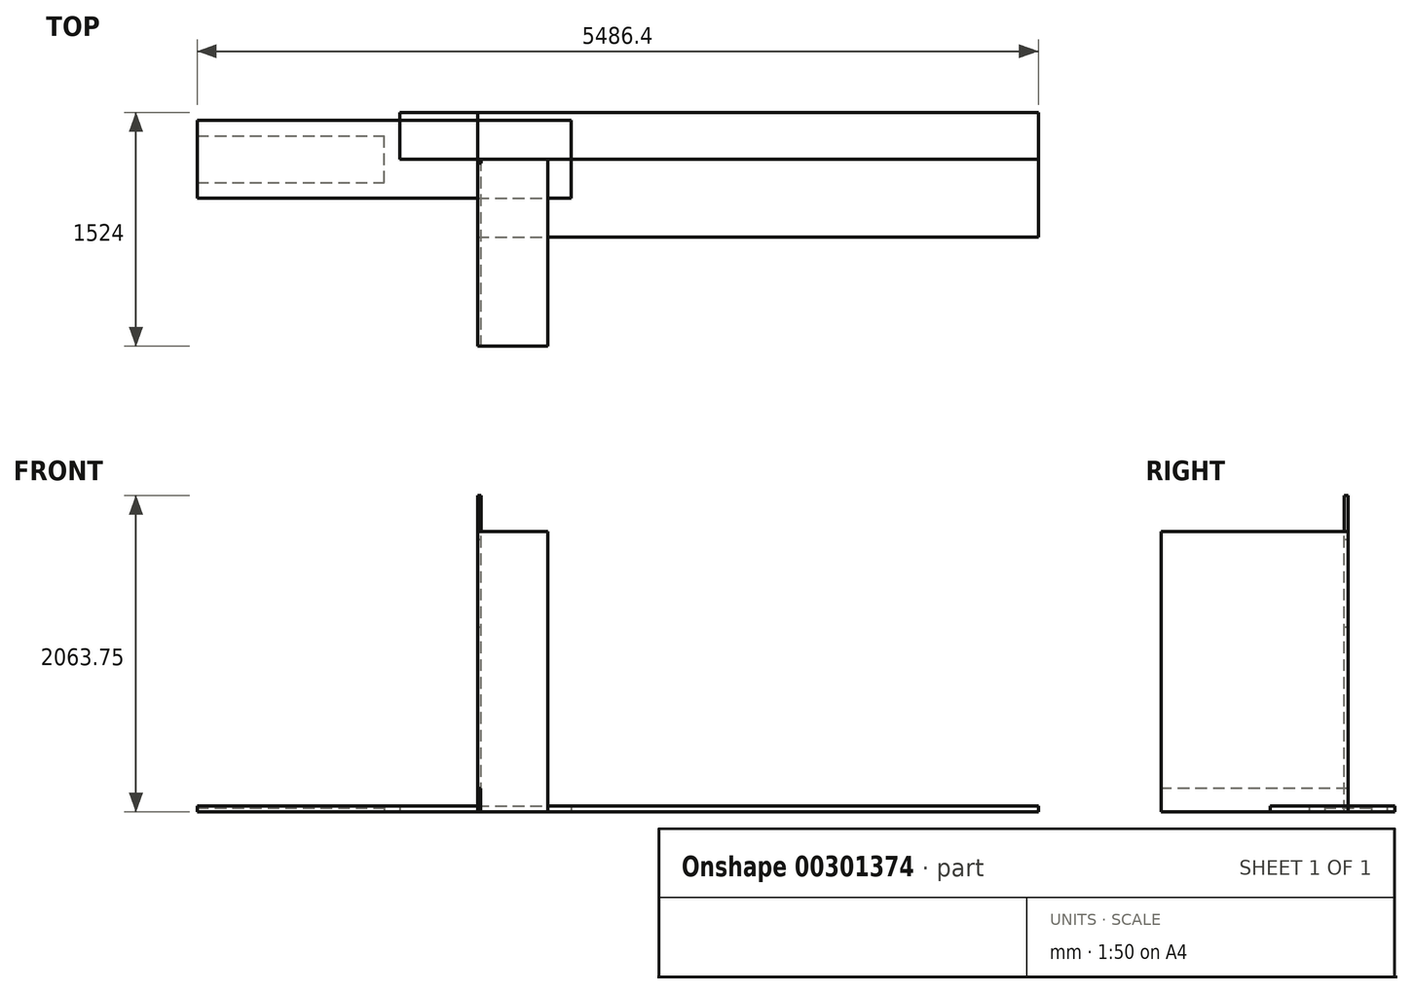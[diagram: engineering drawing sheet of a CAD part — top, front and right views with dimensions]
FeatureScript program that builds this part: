
annotation { "Feature Type Name" : "Feature", "Feature Type Description" : "" }
export const myFeature = defineFeature(function(context is Context, id is Id, definition is map)
    precondition{}
    {
        {
            var Q0;
            Q0=qCreatedBy(makeId("Front.planeOp"),FACE);
            var sketch = newSketch(context, id + "F0", { "sketchPlane" : qUnion([Q0])});
            skLineSegment(sketch, "E0.bottom", {"start": v(0, 0) * mm, "end": v(22.23, 0) * mm});
            skLineSegment(sketch, "E0.top", {"start": v(0, 1778) * mm, "end": v(22.22, 1778) * mm});
            skLineSegment(sketch, "E0.left", {"start": v(0, 0) * mm, "end": v(0, 1778) * mm});
            skLineSegment(sketch, "E0.right", {"start": v(22.23, 0) * mm, "end": v(22.22, 1778) * mm});
            skPoint(sketch, "E1", {"position": v(11.11, 1778) * mm});
            skSolve(sketch);
        }
        {
            var Q0;
            Q0=makeQuery(id+"F0.imprint","IMPRINT",FACE,{"disambiguationData":[TD([[makeQuery(id+"F0.imprint","IMPRINT",EDGE,{"derivedFrom":sQuery(id+"F0.wireOp",EDGE,"E0.bottom")}),1.0]])]});
            extrude(context, id + "F1", {"entities" : qUnion([Q0]), "depth" : 25.4 * mm});
        }
        {
            var Q0;
            Q0=qCreatedBy(makeId("Front.planeOp"),FACE);
            var sketch = newSketch(context, id + "F2", { "sketchPlane" : qUnion([Q0])});
            skLineSegment(sketch, "E2.bottom", {"start": v(0, 0) * mm, "end": v(22.22, 0) * mm});
            skLineSegment(sketch, "E2.top", {"start": v(0, 1206.5) * mm, "end": v(22.22, 1206.5) * mm});
            skLineSegment(sketch, "E2.left", {"start": v(0, 0) * mm, "end": v(0, 1206.5) * mm});
            skLineSegment(sketch, "E2.right", {"start": v(22.22, 0) * mm, "end": v(22.22, 1206.5) * mm});
            skSolve(sketch);
        }
        {
            var Q0;
            Q0 = qSketchRegion(id + "F2", true);
            extrude(context, id + "F3", {"entities" : qUnion([Q0]), "depth" : 25.4 * mm});
        }
        {
            var Q0;
            Q0=qCreatedBy(makeId("Front.planeOp"),FACE);
            var sketch = newSketch(context, id + "F4", { "sketchPlane" : qUnion([Q0])});
            skLineSegment(sketch, "E3.bottom", {"start": v(0, 0) * mm, "end": v(22.23, 0) * mm});
            skLineSegment(sketch, "E3.top", {"start": v(0, 2063.75) * mm, "end": v(22.22, 2063.75) * mm});
            skLineSegment(sketch, "E3.left", {"start": v(0, 0) * mm, "end": v(0, 2063.75) * mm});
            skLineSegment(sketch, "E3.right", {"start": v(22.23, 0) * mm, "end": v(22.22, 2063.75) * mm});
            skSolve(sketch);
        }
        {
            var Q0;
            Q0 = qSketchRegion(id + "F4", true);
            extrude(context, id + "F5", {"entities" : qUnion([Q0]), "depth" : 25.4 * mm});
        }
        {
            var Q0;
            Q0=qCreatedBy(makeId("Top.planeOp"),FACE);
            var sketch = newSketch(context, id + "F6", { "sketchPlane" : qUnion([Q0])});
            skLineSegment(sketch, "E4.bottom", {"start": v(0, 0) * mm, "end": v(3657.6, 0) * mm});
            skLineSegment(sketch, "E4.top", {"start": v(0, -508) * mm, "end": v(3657.6, -508) * mm});
            skLineSegment(sketch, "E4.left", {"start": v(0, 0) * mm, "end": v(0, -508) * mm});
            skLineSegment(sketch, "E4.right", {"start": v(3657.6, 0) * mm, "end": v(3657.6, -508) * mm});
            skSolve(sketch);
        }
        {
            var Q0;
            Q0 = qSketchRegion(id + "F6", true);
            extrude(context, id + "F7", {"entities" : qUnion([Q0]), "depth" : 38.1 * mm});
        }
        {
            var Q0;
            Q0=qCreatedBy(makeId("Top.planeOp"),FACE);
            var sketch = newSketch(context, id + "F8", { "sketchPlane" : qUnion([Q0])});
            skLineSegment(sketch, "E5.bottom", {"start": v(0, 0) * mm, "end": v(3657.6, 0) * mm});
            skLineSegment(sketch, "E5.top", {"start": v(0, 304.8) * mm, "end": v(3657.6, 304.8) * mm});
            skLineSegment(sketch, "E5.left", {"start": v(0, 0) * mm, "end": v(0, 304.8) * mm});
            skLineSegment(sketch, "E5.right", {"start": v(3657.6, 0) * mm, "end": v(3657.6, 304.8) * mm});
            skSolve(sketch);
        }
        {
            var Q0;
            Q0 = qSketchRegion(id + "F8", true);
            extrude(context, id + "F9", {"entities" : qUnion([Q0]), "depth" : 38.1 * mm});
        }
        {
            var Q0;
            Q0=qCreatedBy(makeId("Top.planeOp"),FACE);
            var sketch = newSketch(context, id + "F10", { "sketchPlane" : qUnion([Q0])});
            skLineSegment(sketch, "E6.bottom", {"start": v(-1828.8, 254) * mm, "end": v(609.6, 254) * mm});
            skLineSegment(sketch, "E6.top", {"start": v(-1828.8, -254) * mm, "end": v(609.6, -254) * mm});
            skLineSegment(sketch, "E6.left", {"start": v(-1828.8, 254) * mm, "end": v(-1828.8, -254) * mm});
            skLineSegment(sketch, "E6.right", {"start": v(609.6, 254) * mm, "end": v(609.6, -254) * mm});
            skSolve(sketch);
        }
        {
            var Q0;
            Q0=makeQuery(id+"F10.imprint","IMPRINT",FACE,{"disambiguationData":[TD([[makeQuery(id+"F10.imprint","IMPRINT",EDGE,{"derivedFrom":sQuery(id+"F10.wireOp",EDGE,"E6.bottom")}),-1.0]])]});
            extrude(context, id + "F11", {"entities" : qUnion([Q0]), "depth" : 38.1 * mm});
        }
        {
            var Q0;
            Q0=qCreatedBy(makeId("Top.planeOp"),FACE);
            var sketch = newSketch(context, id + "F12", { "sketchPlane" : qUnion([Q0])});
            skLineSegment(sketch, "E7.bottom", {"start": v(-1828.8, -152.4) * mm, "end": v(-609.6, -152.4) * mm});
            skLineSegment(sketch, "E7.top", {"start": v(-1828.8, 152.4) * mm, "end": v(-609.6, 152.4) * mm});
            skLineSegment(sketch, "E7.left", {"start": v(-1828.8, -152.4) * mm, "end": v(-1828.8, 152.4) * mm});
            skLineSegment(sketch, "E7.right", {"start": v(-609.6, -152.4) * mm, "end": v(-609.6, 152.4) * mm});
            skSolve(sketch);
        }
        {
            var Q0;
            Q0=makeQuery(id+"F12.imprint","IMPRINT",FACE,{"disambiguationData":[TD([[makeQuery(id+"F12.imprint","IMPRINT",EDGE,{"derivedFrom":sQuery(id+"F12.wireOp",EDGE,"E7.bottom")}),1.0]])]});
            extrude(context, id + "F13", {"entities" : qUnion([Q0]), "depth" : 25.4 * mm});
        }
        {
            var Q0;
            Q0=qCreatedBy(makeId("Right.planeOp"),FACE);
            var sketch = newSketch(context, id + "F14", { "sketchPlane" : qUnion([Q0])});
            skLineSegment(sketch, "E8.bottom", {"start": v(0, 0) * mm, "end": v(-1219.2, 0) * mm});
            skLineSegment(sketch, "E8.top", {"start": v(0, 152.4) * mm, "end": v(-1219.2, 152.4) * mm});
            skLineSegment(sketch, "E8.left", {"start": v(0, 0) * mm, "end": v(0, 152.4) * mm});
            skLineSegment(sketch, "E8.right", {"start": v(-1219.2, 0) * mm, "end": v(-1219.2, 152.4) * mm});
            skSolve(sketch);
        }
        {
            var Q0;
            Q0=makeQuery(id+"F14.imprint","IMPRINT",FACE,{"disambiguationData":[TD([[makeQuery(id+"F14.imprint","IMPRINT",EDGE,{"derivedFrom":sQuery(id+"F14.wireOp",EDGE,"E8.bottom")}),-1.0]])]});
            extrude(context, id + "F15", {"entities" : qUnion([Q0]), "depth" : 19.05 * mm});
        }
        {
            var Q0;
            Q0=qCreatedBy(makeId("Right.planeOp"),FACE);
            var sketch = newSketch(context, id + "F16", { "sketchPlane" : qUnion([Q0])});
            skLineSegment(sketch, "E9.bottom", {"start": v(0, 0) * mm, "end": v(-1219.2, 0) * mm});
            skLineSegment(sketch, "E9.top", {"start": v(0, 1828.8) * mm, "end": v(-1219.2, 1828.8) * mm});
            skLineSegment(sketch, "E9.left", {"start": v(0, 0) * mm, "end": v(0, 1828.8) * mm});
            skLineSegment(sketch, "E9.right", {"start": v(-1219.2, 0) * mm, "end": v(-1219.2, 1828.8) * mm});
            skSolve(sketch);
        }
        {
            var Q0;
            Q0 = qSketchRegion(id + "F16", true);
            extrude(context, id + "F17", {"entities" : qUnion([Q0]), "depth" : 457.2 * mm});
        }
        {
            var Q0;
            Q0=qCreatedBy(makeId("Top.planeOp"),FACE);
            var sketch = newSketch(context, id + "F18", { "sketchPlane" : qUnion([Q0])});
            skLineSegment(sketch, "E10.bottom", {"start": v(0, 0) * mm, "end": v(-508, 0) * mm});
            skLineSegment(sketch, "E10.top", {"start": v(0, 304.8) * mm, "end": v(-508, 304.8) * mm});
            skLineSegment(sketch, "E10.left", {"start": v(0, 0) * mm, "end": v(0, 304.8) * mm});
            skLineSegment(sketch, "E10.right", {"start": v(-508, 0) * mm, "end": v(-508, 304.8) * mm});
            skSolve(sketch);
        }
        {
            var Q0;
            Q0 = qSketchRegion(id + "F18", true);
            extrude(context, id + "F19", {"entities" : qUnion([Q0]), "depth" : 38.1 * mm});
        }
    });
